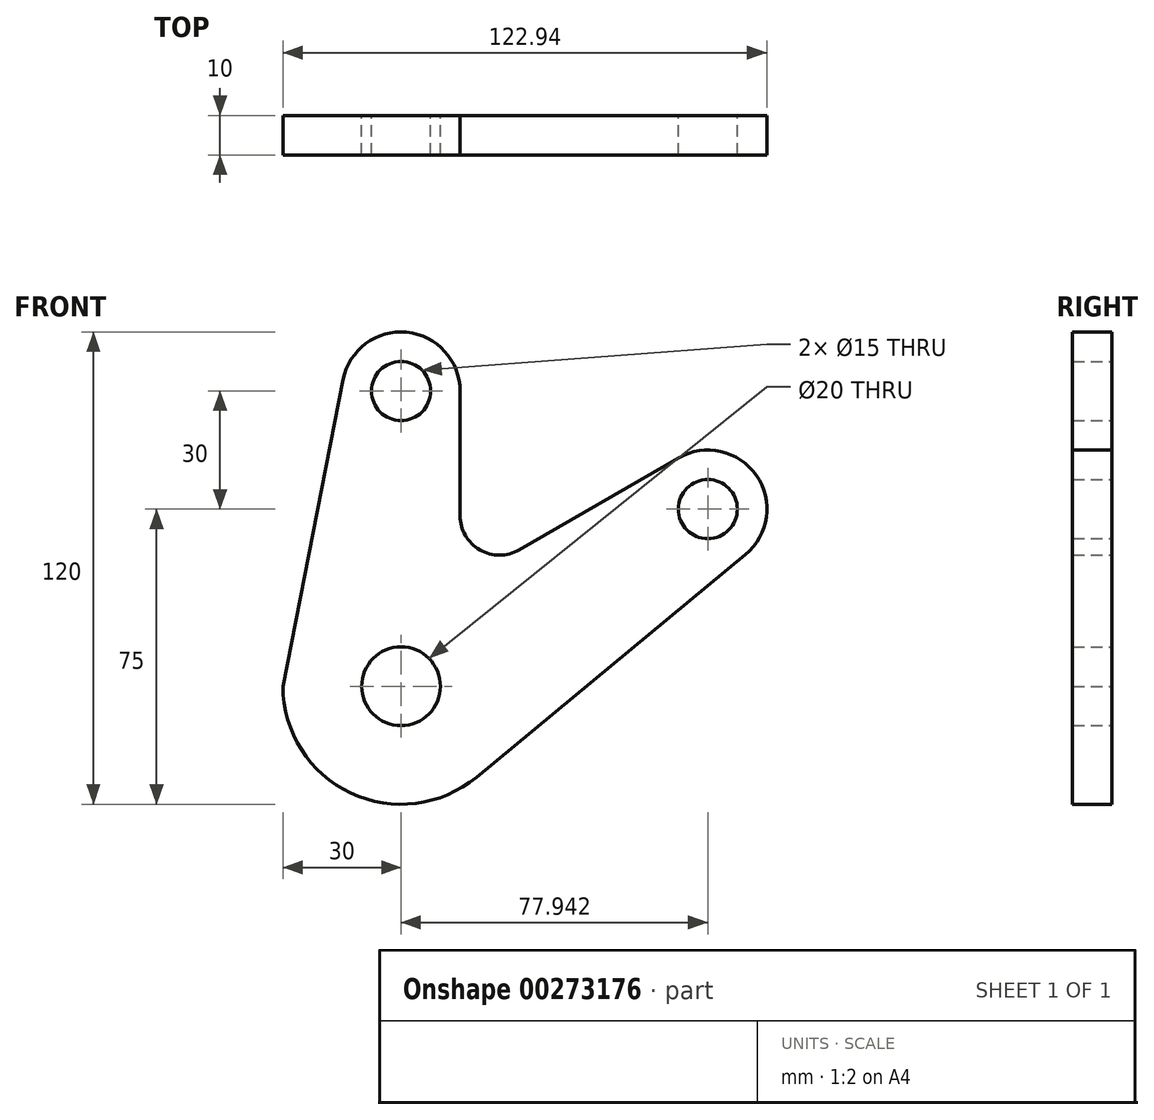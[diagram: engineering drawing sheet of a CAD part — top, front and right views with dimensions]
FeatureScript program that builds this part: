
annotation { "Feature Type Name" : "Feature", "Feature Type Description" : "" }
export const myFeature = defineFeature(function(context is Context, id is Id, definition is map)
    precondition{}
    {
        {
            var Q0;
            Q0=qCreatedBy(makeId("Front.planeOp"),FACE);
            var sketch = newSketch(context, id + "F0", { "sketchPlane" : qUnion([Q0])});
            skCircle(sketch, "E0", {"center": v(0, 0) * mm, "radius": 10 * mm});
            skCircle(sketch, "E1", {"center": v(0, 75) * mm, "radius": 7.5 * mm});
            skCircle(sketch, "E2", {"center": v(77.94, 45) * mm, "radius": 7.5 * mm});
            skArc(sketch, "E3", {"start": v(-30, 0) * mm, "mid": v(-12.77, -27.14) * mm, "end": v(19.12, -23.12) * mm});
            skLineSegment(sketch, "E4", {"start": v(-30, 0) * mm, "end": v(-14.72, 77.89) * mm});
            skArc(sketch, "E5", {"start": v(-14.72, 77.89) * mm, "mid": v(1.45, 89.93) * mm, "end": v(15, 75) * mm});
            skLineSegment(sketch, "E6", {"start": v(15, 75) * mm, "end": v(15, 43.3) * mm});
            skLineSegment(sketch, "E7", {"start": v(19.12, -23.12) * mm, "end": v(87.5, 33.44) * mm});
            skArc(sketch, "E8", {"start": v(87.5, 33.44) * mm, "mid": v(90.26, 53.56) * mm, "end": v(70.44, 58) * mm});
            skLineSegment(sketch, "E9", {"start": v(70.44, 58) * mm, "end": v(30, 34.64) * mm});
            skArc(sketch, "E10", {"start": v(15, 43.3) * mm, "mid": v(20, 34.64) * mm, "end": v(30, 34.64) * mm});
            skLineSegment(sketch, "E11", {"start": v(0, 75) * mm, "end": v(0, 0) * mm, "construction": true});
            skLineSegment(sketch, "E12", {"start": v(0, 0) * mm, "end": v(77.94, 45) * mm, "construction": true});
            skSolve(sketch);
        }
        {
            var Q0;
            Q0 = qSketchRegion(id + "F0", true);
            extrude(context, id + "F1", {"entities" : qUnion([Q0]), "depth" : 10 * mm});
        }
    });
